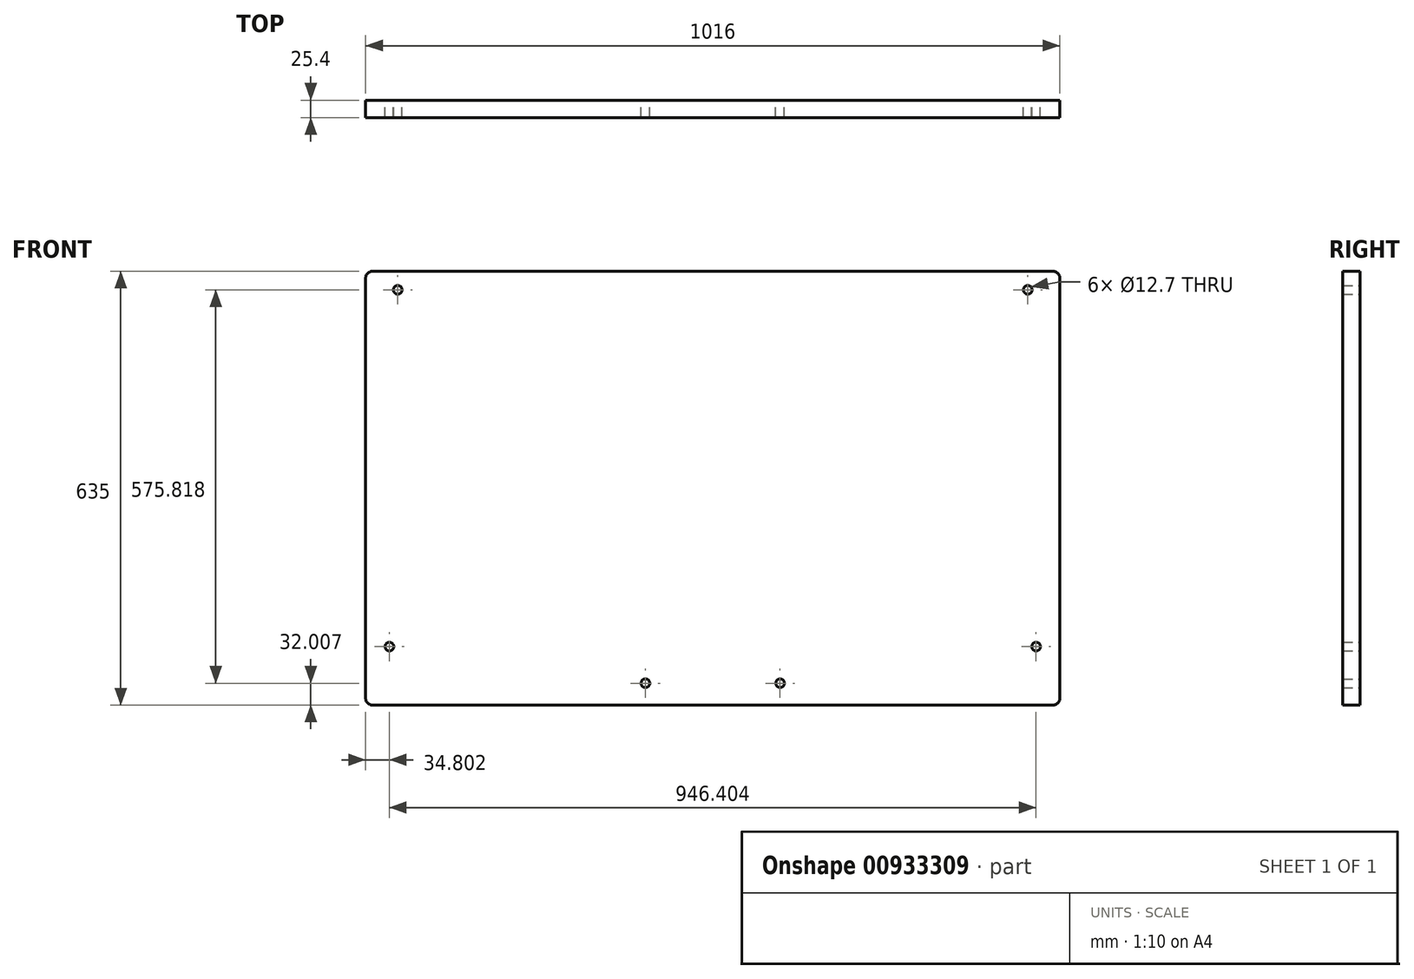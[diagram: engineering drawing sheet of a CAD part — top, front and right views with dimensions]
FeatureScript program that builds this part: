
annotation { "Feature Type Name" : "Feature", "Feature Type Description" : "" }
export const myFeature = defineFeature(function(context is Context, id is Id, definition is map)
    precondition{}
    {
        {
            var Q0;
            Q0=qCreatedBy(makeId("Front.planeOp"),FACE);
            var sketch = newSketch(context, id + "F0", { "sketchPlane" : qUnion([Q0])});
            skLineSegment(sketch, "E0.bottom", {"start": v(-352.98, 352.23) * mm, "end": v(642.7, 352.23) * mm});
            skLineSegment(sketch, "E0.top", {"start": v(-352.98, -282.77) * mm, "end": v(642.7, -282.77) * mm});
            skLineSegment(sketch, "E0.left", {"start": v(-363.14, 342.07) * mm, "end": v(-363.14, -272.6) * mm});
            skLineSegment(sketch, "E0.right", {"start": v(652.86, 342.07) * mm, "end": v(652.86, -272.6) * mm});
            skLineSegment(sketch, "E1", {"start": v(144.86, 352.23) * mm, "end": v(144.86, -282.77) * mm, "construction": true});
            skLineSegment(sketch, "E2", {"start": v(652.86, 199.83) * mm, "end": v(-363.14, 199.83) * mm, "construction": true});
            skCircle(sketch, "E3", {"center": v(-316.15, 325.05) * mm, "radius": 6.35 * mm});
            skCircle(sketch, "E4", {"center": v(-328.34, -197.17) * mm, "radius": 6.35 * mm});
            skCircle(sketch, "E5", {"center": v(46.31, -250.76) * mm, "radius": 6.35 * mm});
            skCircle(sketch, "E6.MirrorC", {"center": v(618.07, -197.17) * mm, "radius": 6.35 * mm});
            skCircle(sketch, "E7.MirrorC", {"center": v(605.87, 325.05) * mm, "radius": 6.35 * mm});
            skCircle(sketch, "E8.MirrorC", {"center": v(243.42, -250.76) * mm, "radius": 6.35 * mm});
            skPoint(sketch, "E9.visualSharp", {"position": v(-363.14, 352.23) * mm});
            skArc(sketch, "E9.filletArc", {"start": v(-352.98, 352.23) * mm, "mid": v(-360.16, 349.26) * mm, "end": v(-363.14, 342.07) * mm});
            skPoint(sketch, "E10.visualSharp", {"position": v(652.86, 352.23) * mm});
            skArc(sketch, "E10.filletArc", {"start": v(652.86, 342.07) * mm, "mid": v(649.89, 349.26) * mm, "end": v(642.7, 352.23) * mm});
            skPoint(sketch, "E11.visualSharp", {"position": v(652.86, -282.77) * mm});
            skArc(sketch, "E11.filletArc", {"start": v(642.7, -282.77) * mm, "mid": v(649.89, -279.8) * mm, "end": v(652.86, -272.6) * mm});
            skPoint(sketch, "E12.visualSharp", {"position": v(-363.14, -282.77) * mm});
            skArc(sketch, "E12.filletArc", {"start": v(-363.14, -272.6) * mm, "mid": v(-360.16, -279.8) * mm, "end": v(-352.98, -282.77) * mm});
            skSolve(sketch);
        }
        {
            var Q0;
            Q0 = qSketchRegion(id + "F0", true);
            extrude(context, id + "F1", {"entities" : qUnion([Q0]), "depth" : 25.4 * mm, "offsetDistance" : 25.4 * mm});
        }
    });
